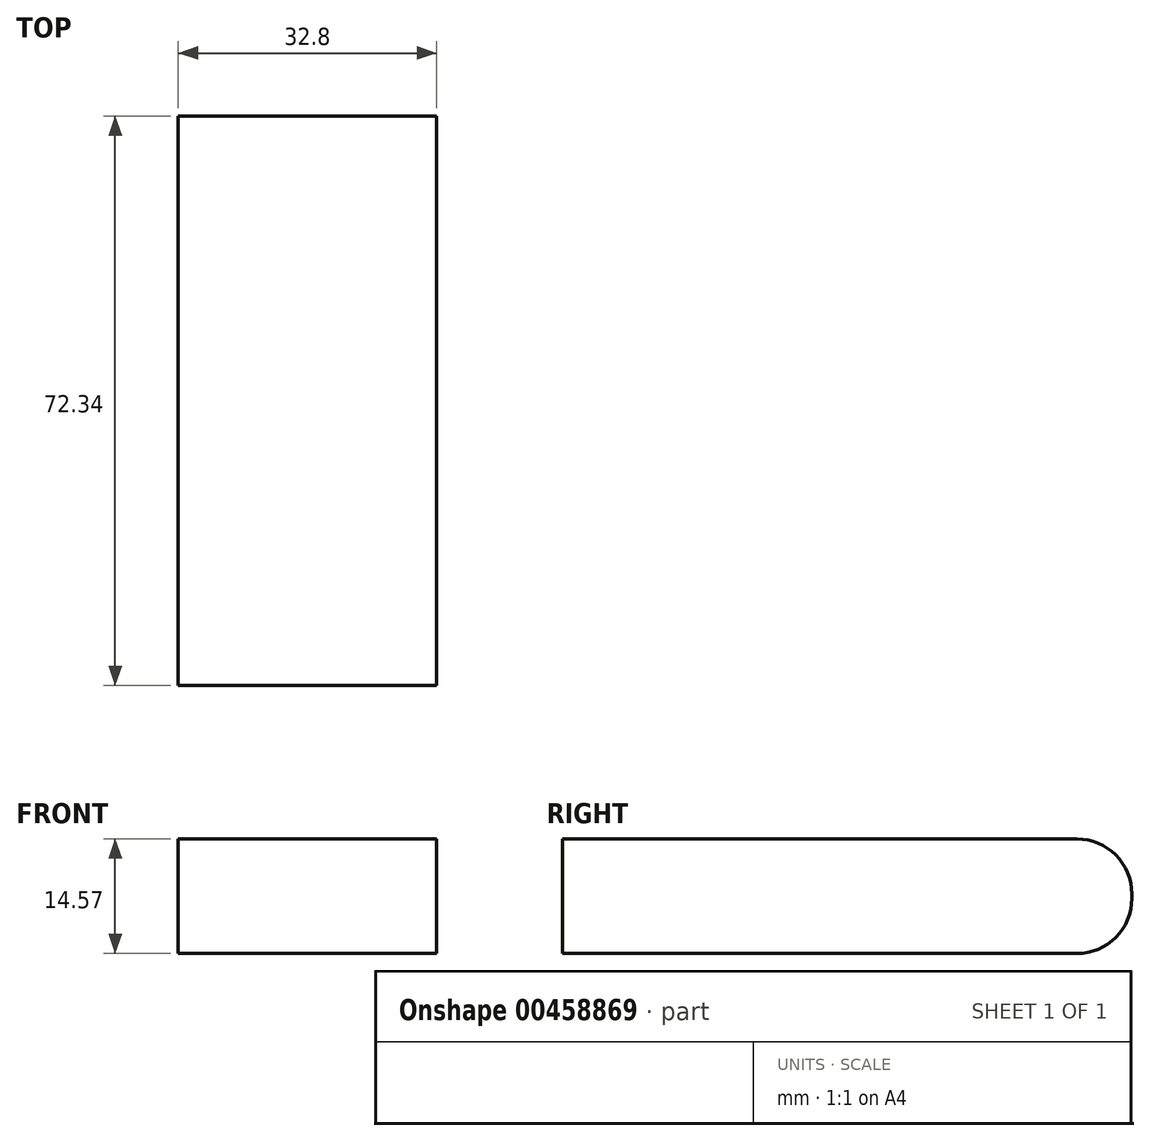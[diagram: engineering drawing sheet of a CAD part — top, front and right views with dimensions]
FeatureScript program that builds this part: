
annotation { "Feature Type Name" : "Feature", "Feature Type Description" : "" }
export const myFeature = defineFeature(function(context is Context, id is Id, definition is map)
    precondition{}
    {
        {
            var Q0;
            Q0=qCreatedBy(makeId("Front.planeOp"),FACE);
            var sketch = newSketch(context, id + "F0", { "sketchPlane" : qUnion([Q0])});
            skLineSegment(sketch, "E0.bottom", {"start": v(0, 0) * mm, "end": v(32.8, 0) * mm});
            skLineSegment(sketch, "E0.top", {"start": v(0, 14.57) * mm, "end": v(32.8, 14.57) * mm});
            skLineSegment(sketch, "E0.left", {"start": v(0, 0) * mm, "end": v(0, 14.57) * mm});
            skLineSegment(sketch, "E0.right", {"start": v(32.8, 0) * mm, "end": v(32.8, 14.57) * mm});
            skSolve(sketch);
        }
        {
            var Q0;
            Q0=makeQuery(id+"F0.imprint","IMPRINT",FACE,{"disambiguationData":[TD([[makeQuery(id+"F0.imprint","IMPRINT",EDGE,{"derivedFrom":sQuery(id+"F0.wireOp",EDGE,"E0.bottom")}),1.0]])]});
            extrude(context, id + "F1", {"entities" : qUnion([Q0]), "depth" : 72.34 * mm, "offsetDistance" : 25 * mm});
        }
        {
            var Q0;
            Q0=makeQuery(id+"F1.opExtrude","CAP_EDGE",EDGE,{"disambiguationData":[OSD([sQuery(id+"F0.wireOp",EDGE,"E0.top")])],"isStart":true});
            var Q1;
            Q1=makeQuery(id+"F1.opExtrude","CAP_EDGE",EDGE,{"disambiguationData":[OSD([sQuery(id+"F0.wireOp",EDGE,"E0.bottom")])],"isStart":true});
            fillet(context, id + "F2", {"entities" : qUnion([Q0, Q1]), "radius" : 7 * mm, "tangentPropagation" : true, "allowEdgeOverflow" : false});
        }
    });
